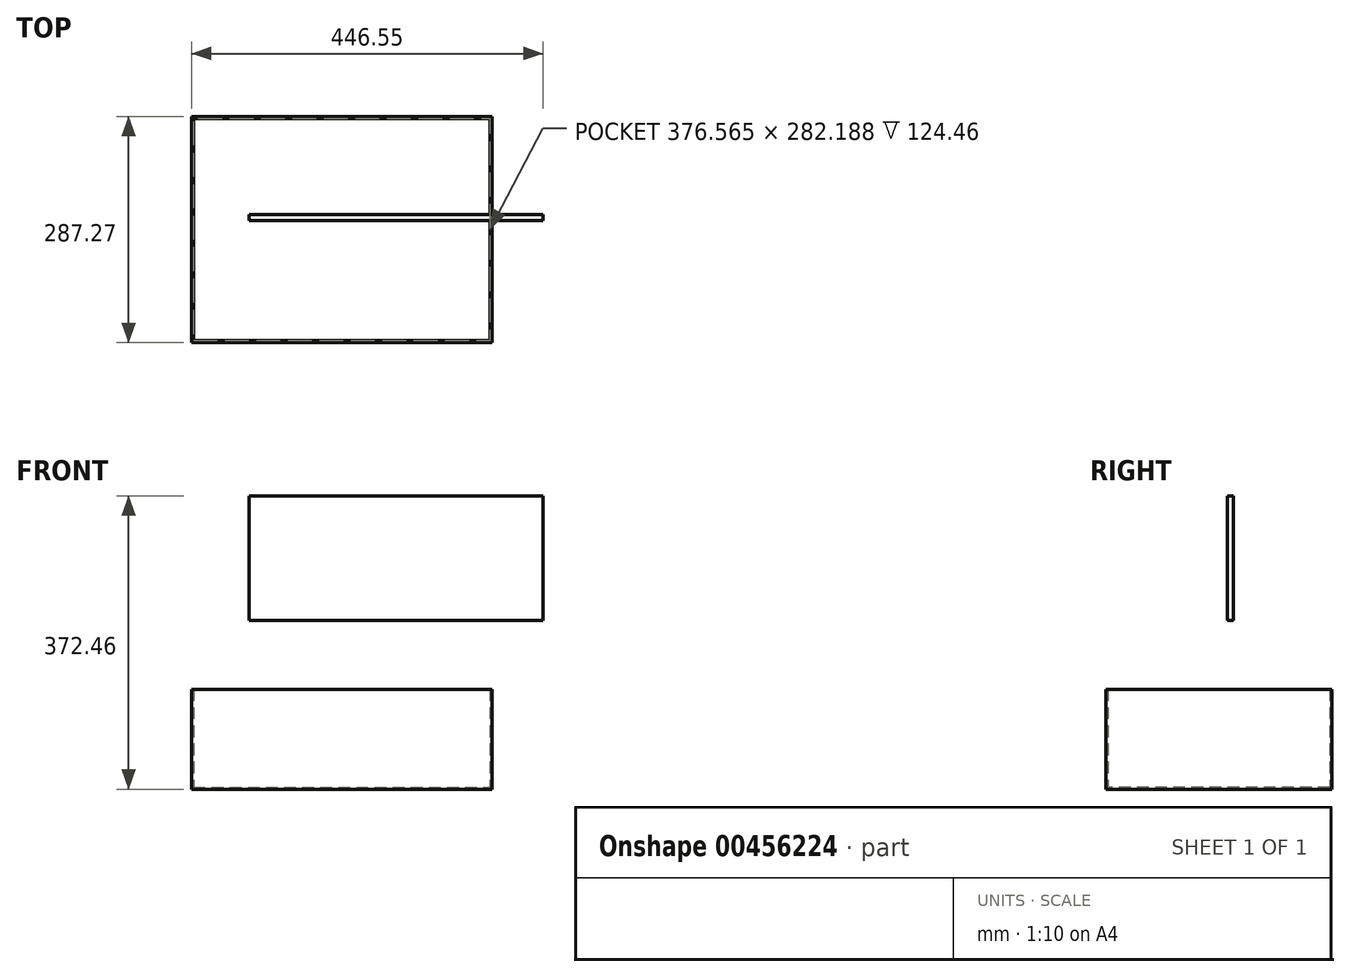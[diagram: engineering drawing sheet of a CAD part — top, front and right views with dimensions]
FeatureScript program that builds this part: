
annotation { "Feature Type Name" : "Feature", "Feature Type Description" : "" }
export const myFeature = defineFeature(function(context is Context, id is Id, definition is map)
    precondition{}
    {
        {
            var Q0;
            Q0=qCreatedBy(makeId("Top.planeOp"),FACE);
            var sketch = newSketch(context, id + "F0", { "sketchPlane" : qUnion([Q0])});
            skLineSegment(sketch, "E0.bottom", {"start": v(-196.1, 124.96) * mm, "end": v(185.55, 124.96) * mm});
            skLineSegment(sketch, "E0.top", {"start": v(-196.1, -162.3) * mm, "end": v(185.55, -162.3) * mm});
            skLineSegment(sketch, "E0.left", {"start": v(-196.1, 124.96) * mm, "end": v(-196.1, -162.3) * mm});
            skLineSegment(sketch, "E0.right", {"start": v(185.55, 124.96) * mm, "end": v(185.55, -162.3) * mm});
            skSolve(sketch);
        }
        {
            var Q0;
            Q0 = qSketchRegion(id + "F0", true);
            extrude(context, id + "F1", {"entities" : qUnion([Q0]), "depth" : 127 * mm});
        }
        {
            var Q0;
            Q0=makeQuery(id+"F1.opExtrude","CAP_FACE",FACE,{"disambiguationData":[OSD([sQuery(id+"F0.wireOp",EDGE,"E0.bottom"),sQuery(id+"F0.wireOp",EDGE,"E0.top"),sQuery(id+"F0.wireOp",EDGE,"E0.left"),sQuery(id+"F0.wireOp",EDGE,"E0.right")])],"isStart":false});
            shell(context, id + "F2", {"entities" : qUnion([Q0]), "thickness" : 2.54 * mm});
        }
        {
            var Q0;
            Q0=qCreatedBy(makeId("Front.planeOp"),FACE);
            var sketch = newSketch(context, id + "F3", { "sketchPlane" : qUnion([Q0])});
            skLineSegment(sketch, "E1.bottom", {"start": v(-122.63, 214.16) * mm, "end": v(250.45, 214.16) * mm});
            skLineSegment(sketch, "E1.top", {"start": v(-122.63, 372.46) * mm, "end": v(250.45, 372.46) * mm});
            skLineSegment(sketch, "E1.left", {"start": v(-122.63, 214.16) * mm, "end": v(-122.63, 372.46) * mm});
            skLineSegment(sketch, "E1.right", {"start": v(250.45, 214.16) * mm, "end": v(250.45, 372.46) * mm});
            skSolve(sketch);
        }
        {
            var Q0;
            Q0 = qSketchRegion(id + "F3", true);
            extrude(context, id + "F4", {"entities" : qUnion([Q0]), "depth" : 7.62 * mm});
        }
    });
